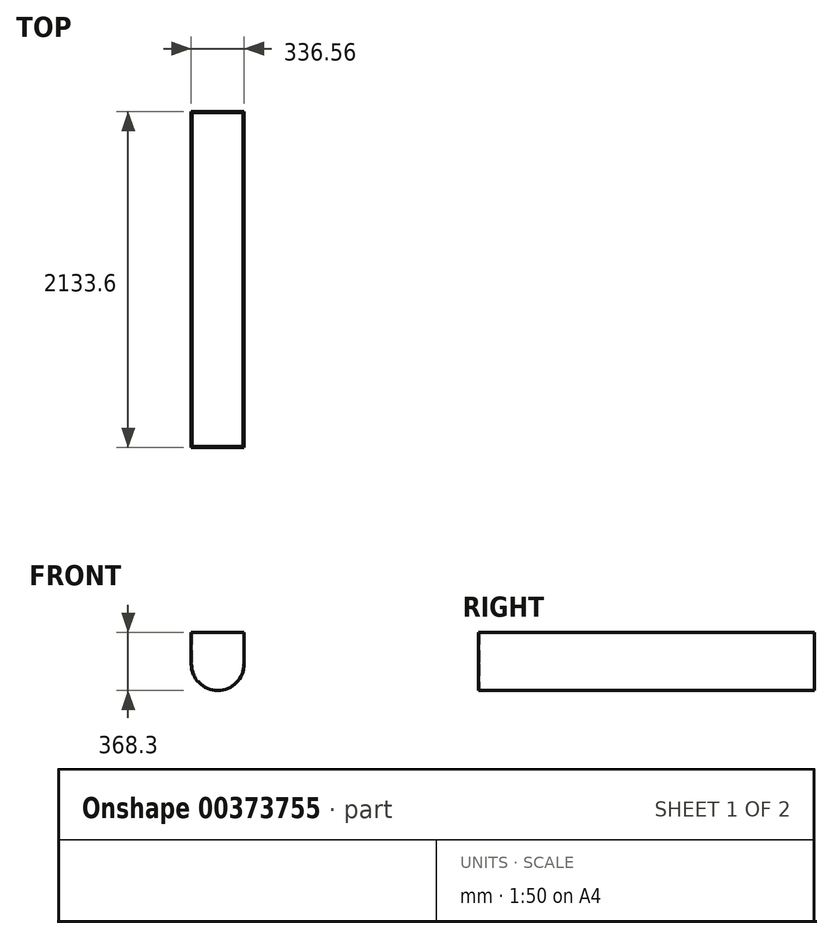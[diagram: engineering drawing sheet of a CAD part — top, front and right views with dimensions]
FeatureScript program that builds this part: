
annotation { "Feature Type Name" : "Feature", "Feature Type Description" : "" }
export const myFeature = defineFeature(function(context is Context, id is Id, definition is map)
    precondition{}
    {
        {
            var Q0;
            Q0=qCreatedBy(makeId("Front.planeOp"),FACE);
            var sketch = newSketch(context, id + "F0", { "sketchPlane" : qUnion([Q0])});
            skLineSegment(sketch, "E0", {"start": v(-168.28, 0) * mm, "end": v(168.28, 0) * mm});
            skLineSegment(sketch, "E1", {"start": v(168.28, 0) * mm, "end": v(168.28, -200.03) * mm});
            skLineSegment(sketch, "E2", {"start": v(-168.28, 0) * mm, "end": v(-168.28, -200.03) * mm});
            skArc(sketch, "E3", {"start": v(-168.27, -200.03) * mm, "mid": v(0, -368.3) * mm, "end": v(168.27, -200.03) * mm});
            skSolve(sketch);
        }
        {
            var Q0;
            Q0 = qSketchRegion(id + "F0", true);
            extrude(context, id + "F1", {"entities" : qUnion([Q0]), "endBound" : BoundingType.SYMMETRIC, "depth" : 2133.6 * mm});
        }
        {
            var Q0;
            Q0=makeQuery(id+"F1.opExtrude","SWEPT_FACE",FACE,{"disambiguationData":[OSD([sQuery(id+"F0.wireOp",EDGE,"E0")])]});
            shell(context, id + "F2", {"entities" : qUnion([Q0]), "thickness" : 6.35 * mm});
        }
    });
